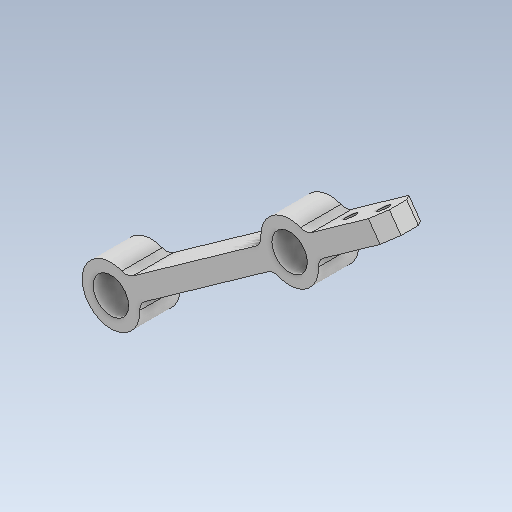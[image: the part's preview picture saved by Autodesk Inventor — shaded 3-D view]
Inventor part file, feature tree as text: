
AUTODESK INVENTOR PART (.ipt)
format: ipt  version: 2020 (Build 240168000, 168)  size: 157,184 bytes
history: native  units: mm
features: other x3, extrude x2, sketch x2, reference x2, fillet x1, chamfer x1, projected_geometry x1
ambient origin geometry x8: Origin, YZ Plane, XZ Plane, XY Plane, X Axis, Y Axis, Z Axis, Center Point
bodies: Solid1 (feature_tree)
feature tree (12):
  extrude  "Extrusion1"  Depth=10.0mm
  extrude  "Extrusion2"  Depth=2.0mm
  fillet  "Fillet1"  Radius=3.5mm
  chamfer  "Chamfer1"  Distance=20.0mm
  sketch  "Sketch1"  dims[d0=10.0mm d1=10.0mm]
  reference  "Reference1"
  reference  "Reference2"
  sketch  "Sketch2"  dims[d2=6.15mm d3=6.15mm d4=3.5mm d5=20.0mm d6=3.5mm d7=7.0mm d8=0.0mm d9=8.0mm d10=5.0mm d11=2.0mm d12=2.0mm d13=2.0mm d14=5.0mm d15=0.0mm d17=2.0mm d18=2.0mm d19=2.0mm d20=45.0deg]
  projected_geometry  "Projected Loop1"
  parser-record x1  (decoder bookkeeping rows leaked as tree rows — omitted from the tree; the rows remain in map.json)
  other  "leg_1.iam"
  other  "leg_holder_2:1"
note: 1 file-system path scrubbed to <path> (originals preserved in map.json)
